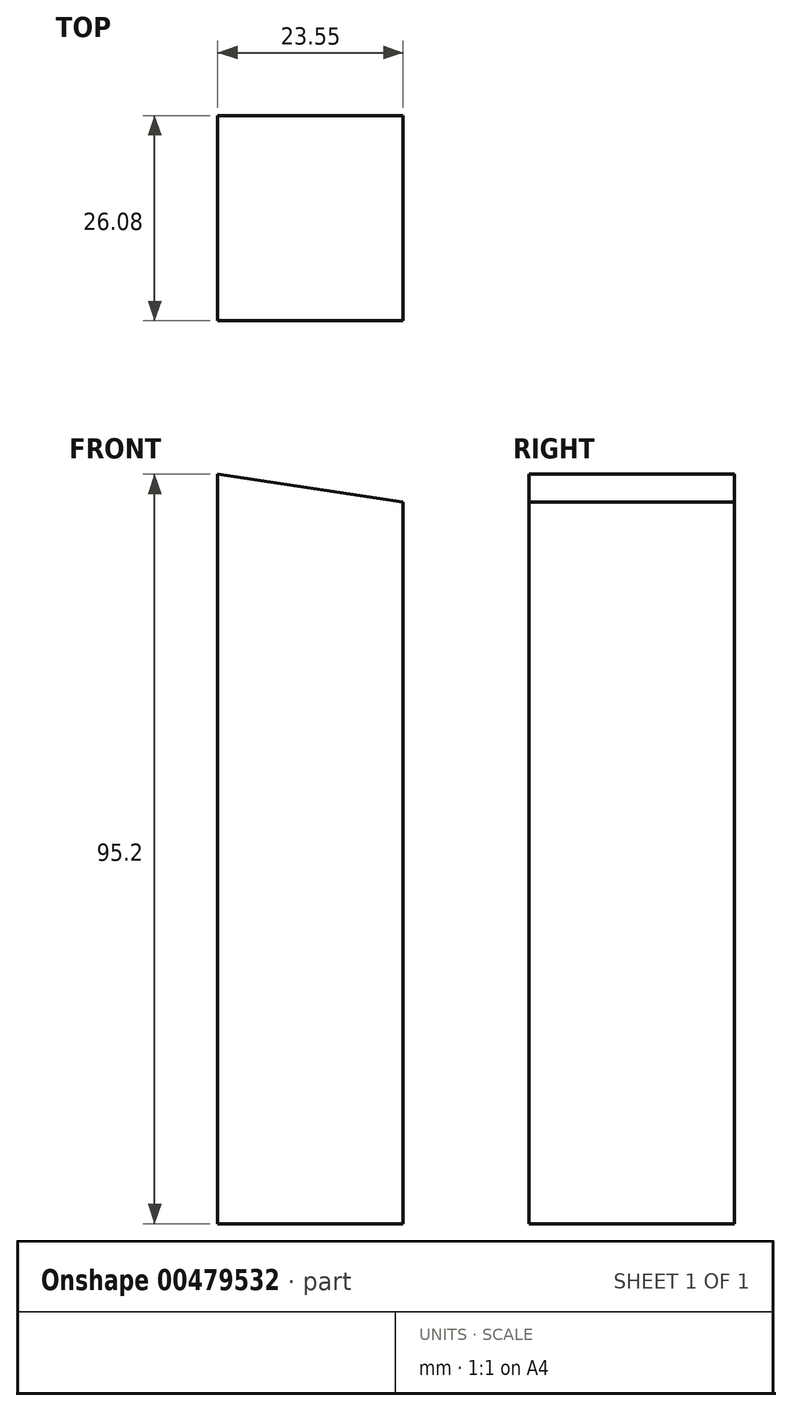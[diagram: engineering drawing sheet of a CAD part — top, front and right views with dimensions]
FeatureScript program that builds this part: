
annotation { "Feature Type Name" : "Feature", "Feature Type Description" : "" }
export const myFeature = defineFeature(function(context is Context, id is Id, definition is map)
    precondition{}
    {
        {
            var Q0;
            Q0=qCreatedBy(makeId("Top.planeOp"),FACE);
            var sketch = newSketch(context, id + "F0", { "sketchPlane" : qUnion([Q0])});
            skLineSegment(sketch, "E0.bottom", {"start": v(-64.92, -35.78) * mm, "end": v(-41.37, -35.78) * mm});
            skLineSegment(sketch, "E0.top", {"start": v(-64.92, -61.86) * mm, "end": v(-41.37, -61.86) * mm});
            skLineSegment(sketch, "E0.left", {"start": v(-64.92, -35.78) * mm, "end": v(-64.92, -61.86) * mm});
            skLineSegment(sketch, "E0.right", {"start": v(-41.37, -35.78) * mm, "end": v(-41.37, -61.86) * mm});
            skSolve(sketch);
        }
        {
            var Q0;
            Q0 = qSketchRegion(id + "F0", true);
            extrude(context, id + "F1", {"entities" : qUnion([Q0]), "depth" : 95.2 * mm, "offsetDistance" : 25 * mm});
        }
        {
            var Q0;
            Q0=makeQuery(id+"F1.opExtrude","SWEPT_FACE",FACE,{"disambiguationData":[OSD([sQuery(id+"F0.wireOp",EDGE,"E0.top")])]});
            var sketch = newSketch(context, id + "F2", { "sketchPlane" : qUnion([Q0])});
            skLineSegment(sketch, "E1", {"start": v(-64.92, 95.2) * mm, "end": v(-41.37, 95.2) * mm});
            skLineSegment(sketch, "E2", {"start": v(-64.92, 95.2) * mm, "end": v(-41.37, 91.68) * mm});
            skLineSegment(sketch, "E3", {"start": v(-41.37, 95.2) * mm, "end": v(-41.37, 91.68) * mm});
            skSolve(sketch);
        }
        {
            var Q0;
            Q0=makeQuery(id+"F2.imprint","IMPRINT",FACE,{"disambiguationData":[TD([[makeQuery(id+"F2.imprint","IMPRINT",EDGE,{"derivedFrom":sQuery(id+"F2.wireOp",EDGE,"E1")}),-1.0]])]});
            extrude(context, id + "F3", {"entities" : qUnion([Q0]), "operationType" : NewBodyOperationType.REMOVE, "oppositeDirection" : true, "depth" : 30 * mm});
        }
    });
